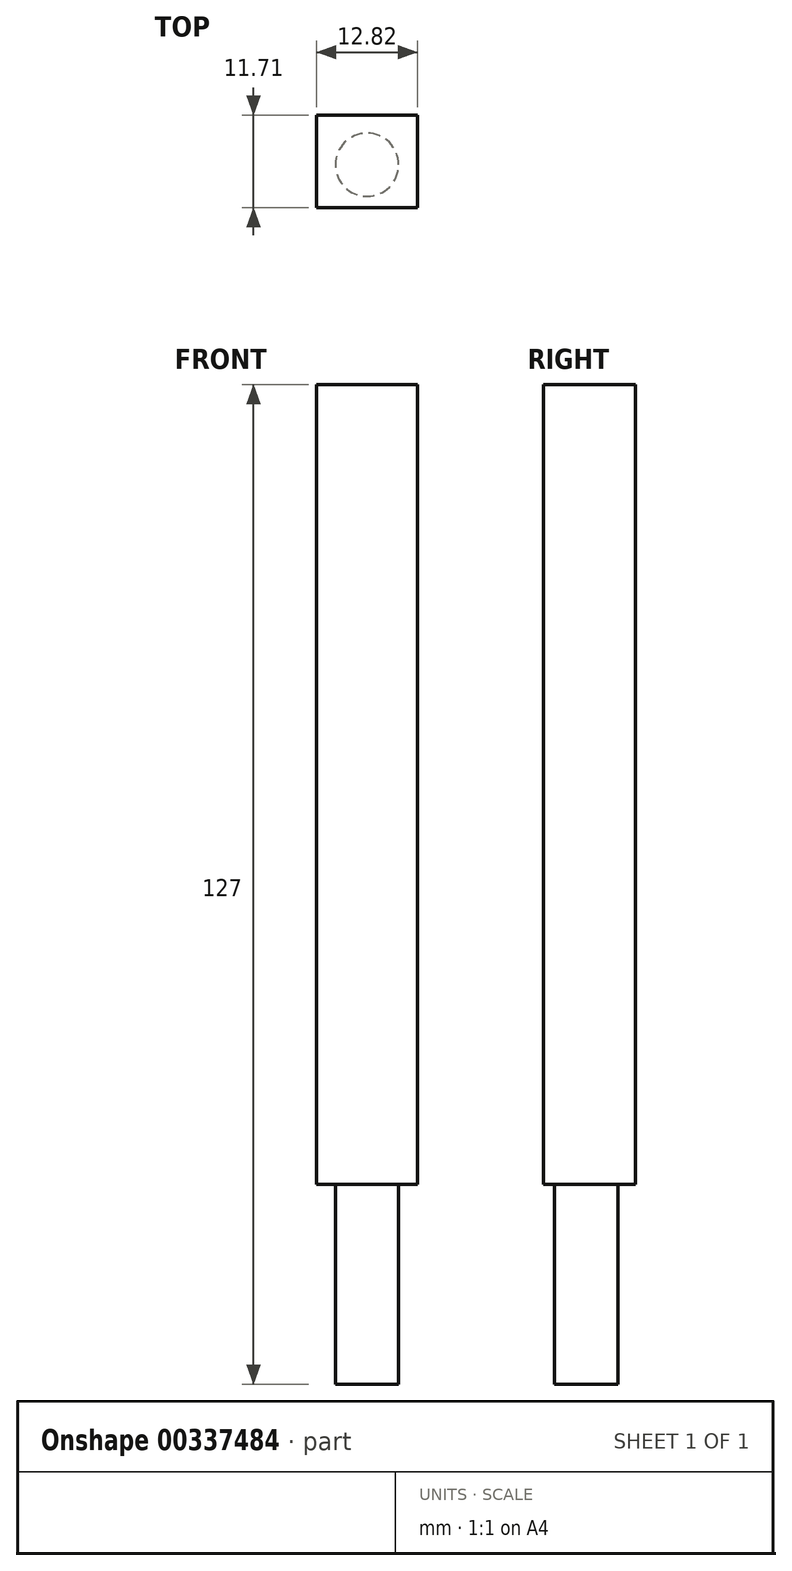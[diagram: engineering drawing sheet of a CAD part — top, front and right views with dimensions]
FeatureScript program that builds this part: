
annotation { "Feature Type Name" : "Feature", "Feature Type Description" : "" }
export const myFeature = defineFeature(function(context is Context, id is Id, definition is map)
    precondition{}
    {
        {
            var Q0;
            Q0=qCreatedBy(makeId("Top.planeOp"),FACE);
            var sketch = newSketch(context, id + "F0", { "sketchPlane" : qUnion([Q0])});
            skLineSegment(sketch, "E0.bottom", {"start": v(0, 0) * mm, "end": v(12.82, 0) * mm});
            skLineSegment(sketch, "E0.top", {"start": v(0, -11.71) * mm, "end": v(12.82, -11.71) * mm});
            skLineSegment(sketch, "E0.left", {"start": v(0, 0) * mm, "end": v(0, -11.71) * mm});
            skLineSegment(sketch, "E0.right", {"start": v(12.82, 0) * mm, "end": v(12.82, -11.71) * mm});
            skSolve(sketch);
        }
        {
            var Q0;
            Q0=makeQuery(id+"F0.imprint","IMPRINT",FACE,{"disambiguationData":[TD([[makeQuery(id+"F0.imprint","IMPRINT",EDGE,{"derivedFrom":sQuery(id+"F0.wireOp",EDGE,"E0.bottom")}),-1.0]])]});
            extrude(context, id + "F1", {"entities" : qUnion([Q0]), "depth" : 101.6 * mm});
        }
        {
            var Q0;
            Q0=qCreatedBy(makeId("Top.planeOp"),FACE);
            var sketch = newSketch(context, id + "F2", { "sketchPlane" : qUnion([Q0])});
            skCircle(sketch, "E1", {"center": v(6.41, -6.29) * mm, "radius": 4.01 * mm});
            skSolve(sketch);
        }
        {
            var Q0;
            Q0=makeQuery(id+"F2.imprint","IMPRINT",FACE,{"disambiguationData":[TD([[makeQuery(id+"F2.imprint","IMPRINT",EDGE,{"derivedFrom":sQuery(id+"F2.wireOp",EDGE,"E1")}),1.0]])]});
            extrude(context, id + "F3", {"entities" : qUnion([Q0]), "operationType" : NewBodyOperationType.ADD, "oppositeDirection" : true, "depth" : 25.4 * mm});
        }
    });
